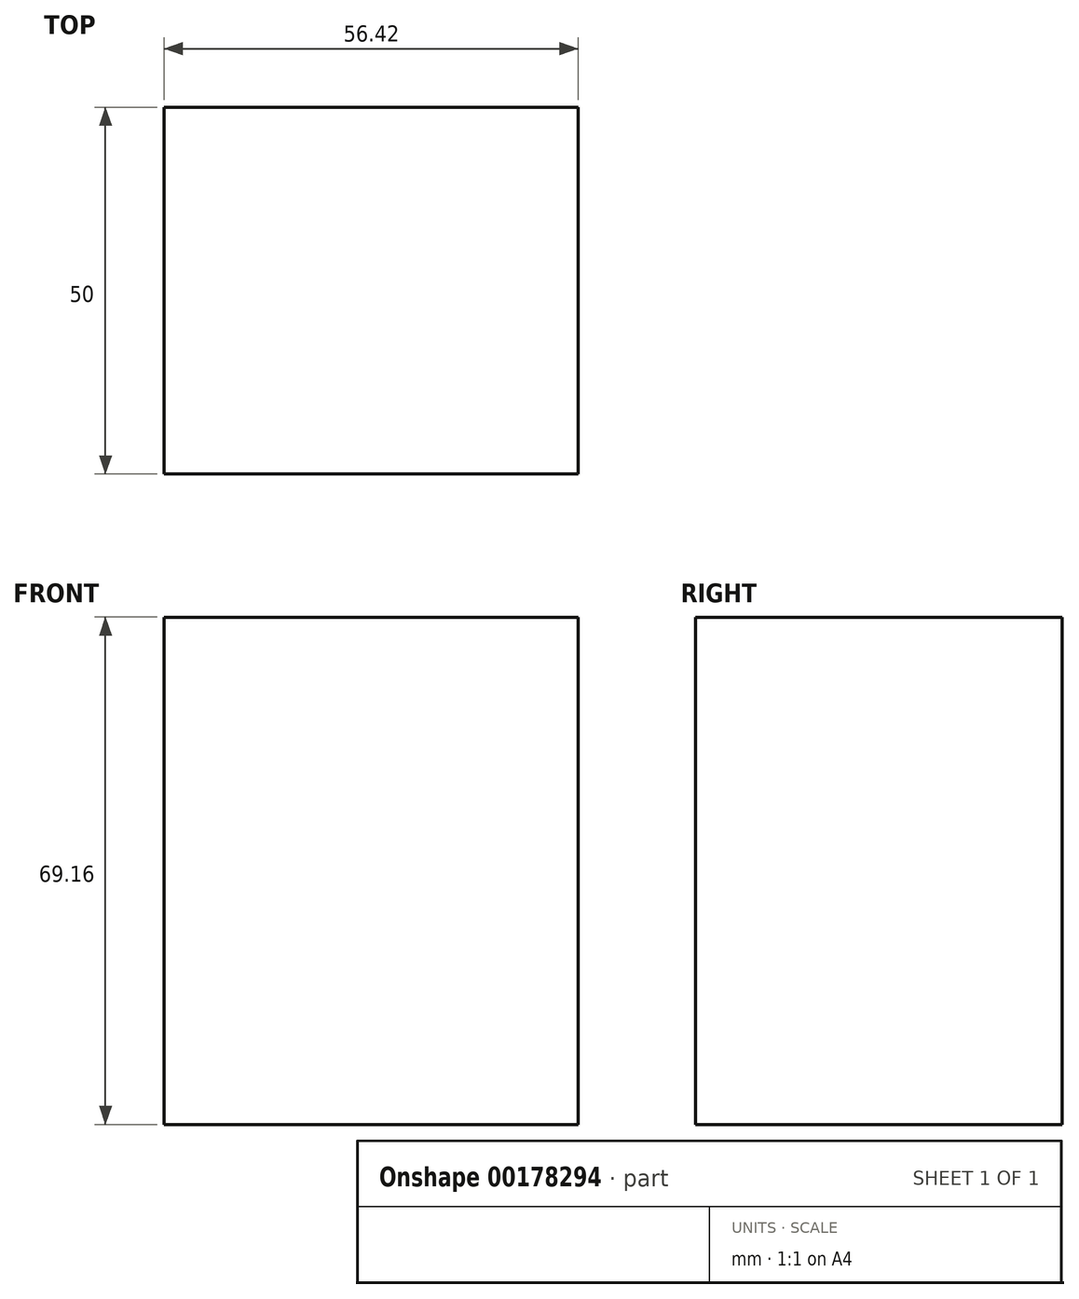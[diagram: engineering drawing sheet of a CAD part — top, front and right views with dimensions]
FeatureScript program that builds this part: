
annotation { "Feature Type Name" : "Feature", "Feature Type Description" : "" }
export const myFeature = defineFeature(function(context is Context, id is Id, definition is map)
    precondition{}
    {
        {
            var Q0;
            Q0=qCreatedBy(makeId("Front.planeOp"),FACE);
            var sketch = newSketch(context, id + "F0", { "sketchPlane" : qUnion([Q0])});
            skLineSegment(sketch, "E0.bottom", {"start": v(0, 0) * mm, "end": v(56.42, 0) * mm});
            skLineSegment(sketch, "E0.top", {"start": v(0, 69.16) * mm, "end": v(56.42, 69.16) * mm});
            skLineSegment(sketch, "E0.left", {"start": v(0, 0) * mm, "end": v(0, 69.16) * mm});
            skLineSegment(sketch, "E0.right", {"start": v(56.42, 0) * mm, "end": v(56.42, 69.16) * mm});
            skSolve(sketch);
        }
        {
            var Q0;
            Q0=makeQuery(id+"F0.imprint","IMPRINT",FACE,{"disambiguationData":[TD([[makeQuery(id+"F0.imprint","IMPRINT",EDGE,{"derivedFrom":sQuery(id+"F0.wireOp",EDGE,"E0.bottom")}),1.0]])]});
            extrude(context, id + "F1", {"entities" : qUnion([Q0]), "depth" : 50 * mm});
        }
    });
